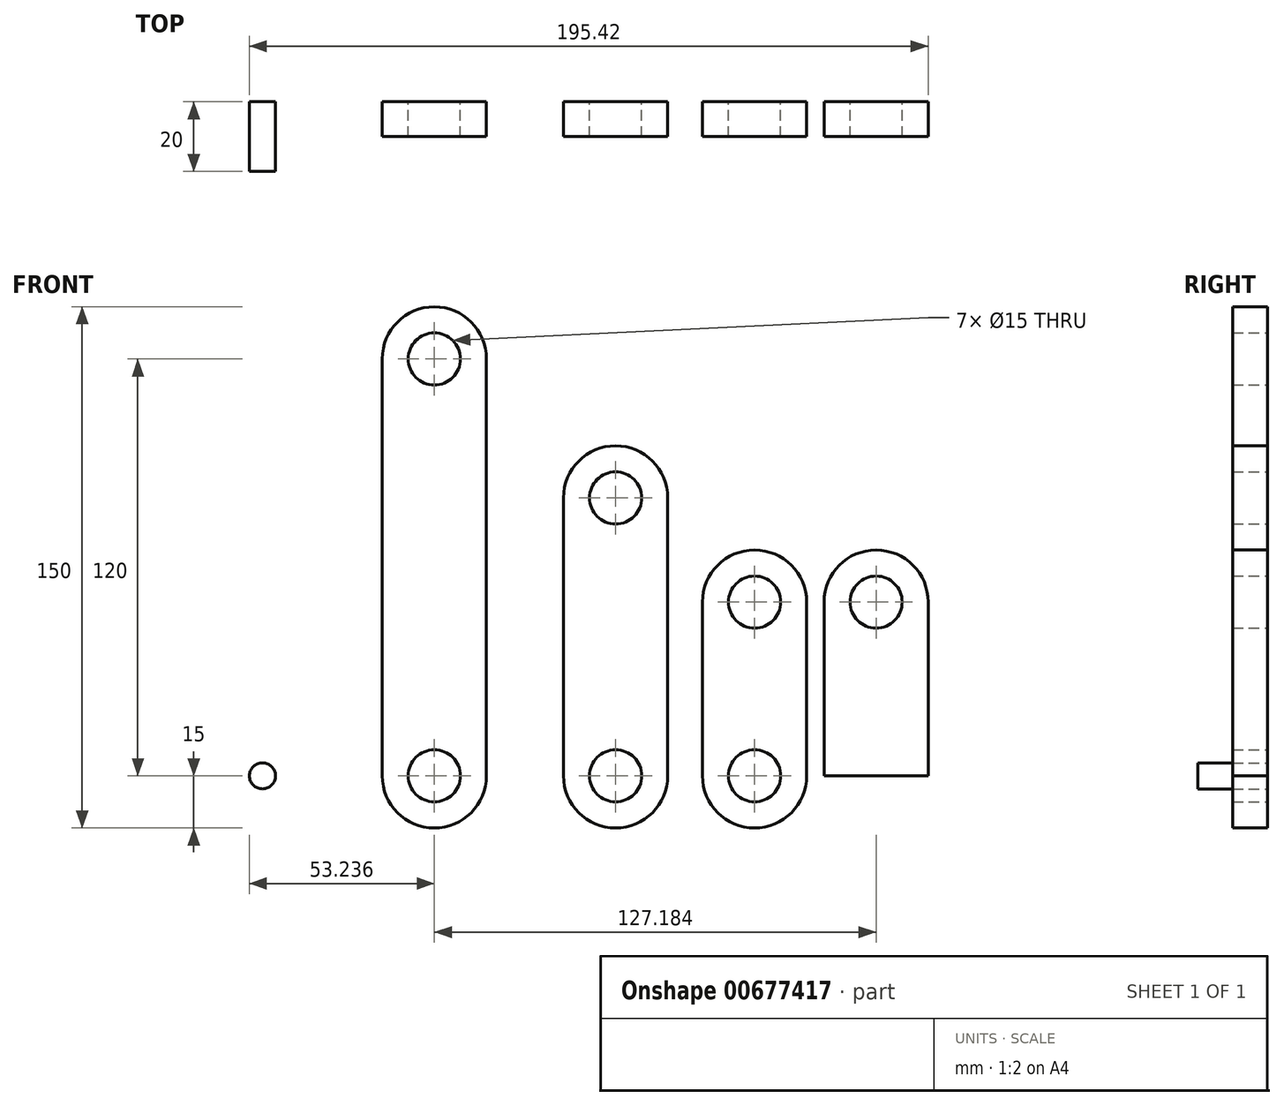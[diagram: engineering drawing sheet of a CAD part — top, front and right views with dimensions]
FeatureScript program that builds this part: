
annotation { "Feature Type Name" : "Feature", "Feature Type Description" : "" }
export const myFeature = defineFeature(function(context is Context, id is Id, definition is map)
    precondition{}
    {
        {
            assignVariable(context, id + "F0", {"name" : "thickness", "anyValue" : 10});
        }
        {
            var Q0;
            Q0=qCreatedBy(makeId("Front.planeOp"),FACE);
            var sketch = newSketch(context, id + "F1", { "sketchPlane" : qUnion([Q0])});
            skLineSegment(sketch, "E0", {"start": v(-10, 0) * mm, "end": v(-40, 0) * mm});
            skLineSegment(sketch, "E1", {"start": v(-40, 0) * mm, "end": v(-40, 50) * mm});
            skLineSegment(sketch, "E2", {"start": v(-10, 0) * mm, "end": v(-10, 50) * mm});
            skCircle(sketch, "E3", {"center": v(-25, 50) * mm, "radius": 15 * mm});
            skPoint(sketch, "E3.centerSnap0", {"position": v(-25, 0) * mm});
            skCircle(sketch, "E4", {"center": v(-25, 50) * mm, "radius": 7.5 * mm});
            skSolve(sketch);
        }
        {
            var Q0;
            Q0=makeQuery(id+"F1.imprint","IMPRINT",FACE,{"disambiguationData":[TD([[makeQuery(id+"F1.imprint","IMPRINT",EDGE,{"derivedFrom":sQuery(id+"F1.wireOp",EDGE,"E4")}),-1.0]])]});
            var Q1;
            Q1=makeQuery(id+"F1.imprint","IMPRINT",FACE,{"disambiguationData":[TD([[makeQuery(id+"F1.imprint","IMPRINT",EDGE,{"derivedFrom":sQuery(id+"F1.wireOp",EDGE,"E0")}),-1.0]])]});
            extrude(context, id + "F2", {"entities" : qUnion([Q0, Q1]), "depth" : (getVariable(context, 'thickness')) * mm, "offsetDistance" : 25 * mm});
        }
        {
            var Q0;
            Q0=qCreatedBy(makeId("Front.planeOp"),FACE);
            var sketch = newSketch(context, id + "F3", { "sketchPlane" : qUnion([Q0])});
            skLineSegment(sketch, "E5", {"start": v(-75, 0) * mm, "end": v(-75, 50) * mm});
            skLineSegment(sketch, "E6", {"start": v(-45, 0) * mm, "end": v(-45, 50) * mm});
            skCircle(sketch, "E7", {"center": v(-60, 50) * mm, "radius": 15 * mm});
            skPoint(sketch, "E7.centerSnap0", {"position": v(-60, 0) * mm});
            skCircle(sketch, "E8", {"center": v(-60, 50) * mm, "radius": 7.5 * mm});
            skCircle(sketch, "E9", {"center": v(-60, 0) * mm, "radius": 15 * mm});
            skCircle(sketch, "E10", {"center": v(-60, 0) * mm, "radius": 7.5 * mm});
            skSolve(sketch);
        }
        {
            var Q0;
            Q0=makeQuery(id+"F3.imprint","IMPRINT",FACE,{"disambiguationData":[TD([[makeQuery(id+"F3.imprint","IMPRINT",EDGE,{"derivedFrom":sQuery(id+"F3.wireOp",EDGE,"E8")}),-1.0]])]});
            var Q1;
            {var subQ0=sQuery(id+"F3.wireOp",EDGE,"E5");Q1=makeQuery(id+"F3.imprint","IMPRINT",FACE,{"disambiguationData":[TD([[makeQuery(id+"F3.imprint","IMPRINT",EDGE,{"derivedFrom":subQ0}),-1.0]])]});}
            var Q2;
            Q2=makeQuery(id+"F3.imprint","IMPRINT",FACE,{"disambiguationData":[TD([[makeQuery(id+"F3.imprint","IMPRINT",EDGE,{"derivedFrom":sQuery(id+"F3.wireOp",EDGE,"E10")}),-1.0]])]});
            extrude(context, id + "F4", {"entities" : qUnion([Q0, Q1, Q2]), "depth" : (getVariable(context, 'thickness')) * mm, "offsetDistance" : 25 * mm});
        }
        {
            var Q0;
            Q0=qCreatedBy(makeId("Front.planeOp"),FACE);
            var sketch = newSketch(context, id + "F5", { "sketchPlane" : qUnion([Q0])});
            skLineSegment(sketch, "E11", {"start": v(-115, 0) * mm, "end": v(-115, 80) * mm});
            skLineSegment(sketch, "E12", {"start": v(-85, 0) * mm, "end": v(-85, 80) * mm});
            skCircle(sketch, "E13", {"center": v(-100, 80) * mm, "radius": 15 * mm});
            skPoint(sketch, "E13.centerSnap0", {"position": v(-100, 0) * mm});
            skCircle(sketch, "E14", {"center": v(-100, 80) * mm, "radius": 7.5 * mm});
            skCircle(sketch, "E15", {"center": v(-100, 0) * mm, "radius": 15 * mm});
            skCircle(sketch, "E16", {"center": v(-100, 0) * mm, "radius": 7.5 * mm});
            skSolve(sketch);
        }
        {
            var Q0;
            {var subQ0=sQuery(id+"F5.wireOp",EDGE,"E11");Q0=makeQuery(id+"F5.imprint","IMPRINT",FACE,{"disambiguationData":[TD([[makeQuery(id+"F5.imprint","IMPRINT",EDGE,{"derivedFrom":subQ0}),-1.0]])]});}
            var Q1;
            Q1=makeQuery(id+"F5.imprint","IMPRINT",FACE,{"disambiguationData":[TD([[makeQuery(id+"F5.imprint","IMPRINT",EDGE,{"derivedFrom":sQuery(id+"F5.wireOp",EDGE,"E14")}),-1.0]])]});
            var Q2;
            Q2=makeQuery(id+"F5.imprint","IMPRINT",FACE,{"disambiguationData":[TD([[makeQuery(id+"F5.imprint","IMPRINT",EDGE,{"derivedFrom":sQuery(id+"F5.wireOp",EDGE,"E16")}),-1.0]])]});
            extrude(context, id + "F6", {"entities" : qUnion([Q0, Q1, Q2]), "depth" : (getVariable(context, 'thickness')) * mm, "offsetDistance" : 25 * mm});
        }
        {
            var Q0;
            Q0=qCreatedBy(makeId("Front.planeOp"),FACE);
            var sketch = newSketch(context, id + "F7", { "sketchPlane" : qUnion([Q0])});
            skLineSegment(sketch, "E17", {"start": v(-167.18, 0) * mm, "end": v(-167.18, 120) * mm});
            skLineSegment(sketch, "E18", {"start": v(-137.18, 0) * mm, "end": v(-137.18, 120) * mm});
            skCircle(sketch, "E19", {"center": v(-152.18, 120) * mm, "radius": 15 * mm});
            skPoint(sketch, "E19.centerSnap0", {"position": v(-152.18, 0) * mm});
            skCircle(sketch, "E20", {"center": v(-152.18, 120) * mm, "radius": 7.5 * mm});
            skCircle(sketch, "E21", {"center": v(-152.18, 0) * mm, "radius": 15 * mm});
            skCircle(sketch, "E22", {"center": v(-152.18, 0) * mm, "radius": 7.5 * mm});
            skSolve(sketch);
        }
        {
            var Q0;
            Q0=makeQuery(id+"F7.imprint","IMPRINT",FACE,{"disambiguationData":[TD([[makeQuery(id+"F7.imprint","IMPRINT",EDGE,{"derivedFrom":sQuery(id+"F7.wireOp",EDGE,"E20")}),-1.0]])]});
            var Q1;
            {var subQ0=sQuery(id+"F7.wireOp",EDGE,"E17");Q1=makeQuery(id+"F7.imprint","IMPRINT",FACE,{"disambiguationData":[TD([[makeQuery(id+"F7.imprint","IMPRINT",EDGE,{"derivedFrom":subQ0}),-1.0]])]});}
            var Q2;
            Q2=makeQuery(id+"F7.imprint","IMPRINT",FACE,{"disambiguationData":[TD([[makeQuery(id+"F7.imprint","IMPRINT",EDGE,{"derivedFrom":sQuery(id+"F7.wireOp",EDGE,"E22")}),-1.0]])]});
            extrude(context, id + "F8", {"entities" : qUnion([Q0, Q1, Q2]), "depth" : (getVariable(context, 'thickness')) * mm, "offsetDistance" : 25 * mm});
        }
        {
            var Q0;
            Q0=qCreatedBy(makeId("Front.planeOp"),FACE);
            var sketch = newSketch(context, id + "F9", { "sketchPlane" : qUnion([Q0])});
            skCircle(sketch, "E23", {"center": v(-201.67, 0) * mm, "radius": 3.75 * mm});
            skSolve(sketch);
        }
        {
            var Q0;
            Q0=makeQuery(id+"F9.imprint","IMPRINT",FACE,{"disambiguationData":[TD([[makeQuery(id+"F9.imprint","IMPRINT",EDGE,{"derivedFrom":sQuery(id+"F9.wireOp",EDGE,"E23")}),1.0]])]});
            extrude(context, id + "F10", {"entities" : qUnion([Q0]), "depth" : (getVariable(context, 'thickness') * 2) * mm, "offsetDistance" : 25 * mm});
        }
    });
